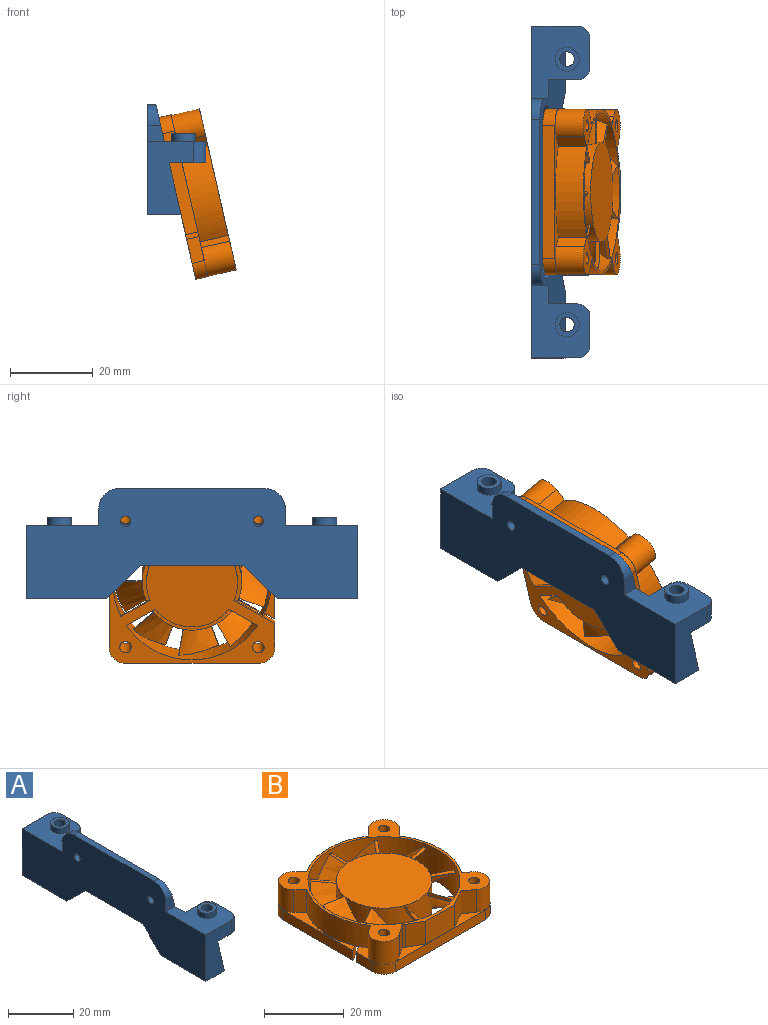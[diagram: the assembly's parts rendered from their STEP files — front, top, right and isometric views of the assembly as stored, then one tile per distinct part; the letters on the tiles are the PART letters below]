
ASSEMBLY  parts=2 mates=1
PART A: 45 faces, bbox 14.7x80.1x28.5 mm
  f0: plane 80.12x26.62mm, normal (-1,0,0), area 1520.2mm2, adj f2,f3,f6,f7,f8,f9,f10,f11
  f1: plane 80x26.5mm, normal (0.97,0,0.22), area 1152.6mm2, adj f2,f3,f6,f10,f11,f12,f13,f14
  f2: plane 17.5x14mm, normal (0,0,1), area 169.7mm2, adj f0,f1,f12,f13,f20,f21,f28,f41
  f3: plane 17.5x14mm, normal (0,0,1), area 169.7mm2, adj f0,f1,f6,f10,f16,f18,f26,f43
  f4: cylinder r=1.75mm len=4.5mm, axis (0,0,1), area 49.5mm2, adj f25,f29
  f5: cylinder r=1.75mm len=4.5mm, axis (0,0,1), area 49.5mm2, adj f22,f27
  f6: plane 17.5x11mm, normal (0,-1,0), area 137.1mm2, adj f0,f1,f3,f15,f17,f43
  f7: plane 8.01x8.01mm, normal (0,0.71,-0.71), area 53.3mm2, adj f0,f8,f15,f37,f38
  f8: plane 25x3.66mm, normal (0,0,-1), area 91.6mm2, adj f0,f7,f9,f37
  f9: plane 8.01x8.01mm, normal (0,-0.71,-0.71), area 53.3mm2, adj f0,f8,f11,f36,f37
  f10: plane 4x4mm, normal (0,-1,0), area 14.2mm2, adj f0,f1,f3,f35
  f11: plane 19.5x8mm, normal (0,0,-1), area 154.2mm2, adj f0,f1,f9,f12,f36
  f12: plane 17.5x11mm, normal (0,1,0), area 137.1mm2, adj f0,f1,f2,f11,f19,f42
  f13: plane 4x4mm, normal (0,1,0), area 14.2mm2, adj f0,f1,f2,f34
  f14: plane 35x1.94mm, normal (0,0,1), area 68mm2, adj f0,f1,f34,f35
  f15: plane 19.5x8mm, normal (0,0,-1), area 154.2mm2, adj f0,f1,f6,f7,f38
  f16: plane 7x5mm, normal (0,1,0), area 32.1mm2, adj f1,f3,f17,f44
  f17: plane 13x8.86mm, normal (0,0,-1), area 78.1mm2, adj f1,f6,f16,f18,f23,f43,f44
  f18: plane 7x5mm, normal (1,0,0), area 35mm2, adj f3,f17,f43,f44
  f19: plane 13x8.86mm, normal (0,0,-1), area 78.1mm2, adj f1,f12,f20,f21,f24,f41,f42
  f20: plane 7x5mm, normal (0,-1,0), area 32.1mm2, adj f1,f2,f19,f41
  f21: plane 7x5mm, normal (1,0,0), area 35mm2, adj f2,f19,f41,f42
  f22: plane 6.5x6.5mm, normal (0,0,-1), area 23.6mm2, adj f5,f23
  f23: cylinder r=3.25mm len=6.5mm, axis (0,0,-1), area 51.1mm2, adj f17,f22
  f24: cylinder r=3.25mm len=6.5mm, axis (0,0,-1), area 51.1mm2, adj f19,f25
  f25: plane 6.5x6.5mm, normal (0,0,-1), area 23.6mm2, adj f4,f24
  f26: cylinder r=2.9mm len=5.8mm, axis (0,0,-1), area 36.4mm2, adj f3,f27
  f27: plane 5.8x5.8mm, normal (0,0,1), area 16.8mm2, adj f5,f26
  f28: cylinder r=2.9mm len=5.8mm, axis (0,0,-1), area 36.4mm2, adj f2,f29
  f29: plane 5.8x5.8mm, normal (0,0,1), area 16.8mm2, adj f4,f28
  f30: cylinder r=5mm len=10.24mm, axis (0.97,0,0.22), area 69.1mm2, adj f1,f31
  f31: plane 10x9.75mm, normal (0.97,0,0.22), area 73.6mm2, adj f30,f40
  f32: cylinder r=5mm len=10.24mm, axis (0.97,0,0.22), area 69.1mm2, adj f1,f33
  f33: plane 10x9.75mm, normal (0.97,0,0.22), area 73.6mm2, adj f32,f39
  f34: cylinder r=5mm len=5mm, axis (-1,0,0), area 18.5mm2, adj f0,f1,f13,f14
  f35: cylinder r=5mm len=5mm, axis (-1,0,0), area 18.5mm2, adj f0,f1,f10,f14
  f36: cylinder r=2mm len=12.31mm, axis (-0.16,-0.7,0.7), area 44.3mm2, adj f1,f9,f11,f37
  f37: cylinder r=2mm len=26.66mm, axis (0,-1,0), area 91.6mm2, adj f1,f7,f8,f9,f36,f38
  f38: cylinder r=2mm len=12.31mm, axis (0.16,-0.7,-0.7), area 44.3mm2, adj f1,f7,f15,f37
  f39: cylinder r=1.25mm len=2.82mm, axis (0.97,0,0.22), area 11.4mm2, adj f0,f33
  f40: cylinder r=1.25mm len=2.82mm, axis (0.97,0,0.22), area 11.4mm2, adj f0,f31
  f41: cylinder r=3mm len=5mm, axis (0,0,-1), area 23.6mm2, adj f2,f19,f20,f21
  f42: cylinder r=3mm len=5mm, axis (0,0,1), area 23.6mm2, adj f2,f12,f19,f21
  f43: cylinder r=3mm len=5mm, axis (0,0,-1), area 23.6mm2, adj f3,f6,f17,f18
  f44: cylinder r=3mm len=5mm, axis (0,0,1), area 23.6mm2, adj f3,f16,f17,f18
PART B: 104 faces, bbox 40x40x10 mm
  f0: plane 4.98x4.18mm, normal (0.64,0.77,0), area 6.5mm2, adj f2,f3,f4,f24
  f1: plane 6.11x2.22mm, normal (-0.94,-0.34,0), area 6.5mm2, adj f2,f3,f4,f5
  f2: bspline ~9x7.84mm, area 9.7mm2, adj f0,f1,f3,f4
  f3: bspline ~10.07x9.67mm, area 73.6mm2, adj f0,f1,f2,f24
  f4: bspline ~10.07x9.67mm, area 73.6mm2, adj f0,f1,f2,f5
  f5: cylinder r=12mm len=13.3mm, axis (0,0,-1), area 69.1mm2, adj f1,f4,f6,f9,f74,f75
  f6: plane 6.4x1.13mm, normal (0.98,0.17,0), area 6.5mm2, adj f5,f8,f9,f10
  f7: plane 6.11x2.22mm, normal (-0.94,0.34,0), area 6.5mm2, adj f8,f9,f10,f11
  f8: bspline ~9.54x9mm, area 9.7mm2, adj f6,f7,f9,f10
  f9: bspline ~9.54x8mm, area 73.6mm2, adj f5,f6,f7,f8
  f10: bspline ~9.54x8mm, area 73.6mm2, adj f6,f7,f8,f11
  f11: cylinder r=12mm len=12.48mm, axis (0,0,-1), area 69.1mm2, adj f7,f10,f12,f15,f74,f75
  f12: plane 5.63x3.25mm, normal (0.87,-0.5,0), area 6.5mm2, adj f11,f14,f15,f16
  f13: plane 5.63x3.25mm, normal (-0.5,0.87,0), area 6.5mm2, adj f14,f15,f16,f17
  f14: bspline ~9x6.77mm, area 9.7mm2, adj f12,f13,f15,f16
  f15: bspline ~10.02x10.02mm, area 73.6mm2, adj f11,f12,f13,f14
  f16: bspline ~10.02x10.02mm, area 73.6mm2, adj f12,f13,f14,f17
  f17: cylinder r=12mm len=12.48mm, axis (0,0,-1), area 69.1mm2, adj f13,f16,f18,f21,f25,f74,f75,f76
  f18: plane 6.11x2.22mm, normal (0.34,-0.94,0), area 6.5mm2, adj f17,f20,f21,f22
  f19: plane 6.4x1.13mm, normal (0.17,0.98,0), area 6.5mm2, adj f20,f21,f22,f24
  f20: bspline ~9.54x9mm, area 9.7mm2, adj f18,f19,f21,f22
  f21: bspline ~9.54x8mm, area 73.6mm2, adj f17,f18,f19,f20
  f22: bspline ~9.54x8mm, area 73.6mm2, adj f18,f19,f20,f24
  f23: plane 5.9x3mm, normal (-1,0,0), area 17.7mm2, adj f39,f40,f52,f72
  f24: cylinder r=12mm len=24mm, axis (0,0,-1), area 416.7mm2, adj f0,f3,f19,f22,f26,f27,f73,f74
  f25: plane 7.42x5.73mm, normal (0,0,1), area 17.8mm2, adj f17,f28,f71,f72
  f26: plane 7.42x5.73mm, normal (0,0,1), area 17.8mm2, adj f24,f28,f69,f70
  f27: plane 7.17x2.5mm, normal (0,0,1), area 17.8mm2, adj f24,f28,f66,f67
  f28: cylinder r=19.1mm len=38.2mm, axis (0,0,1), area 1189.6mm2, adj f25,f26,f27,f33,f40,f66,f67,f69
  f29: cylinder r=11mm len=17.68mm, axis (0,0,-1), area 20.5mm2, adj f40,f70,f71,f74
  f30: cylinder r=11mm len=15.31mm, axis (0,0,-1), area 20.5mm2, adj f40,f67,f69,f73
  f31: plane 32x3mm, normal (0,1,0), area 96mm2, adj f36,f38,f40,f52
  f32: plane 32x3mm, normal (0,-1,0), area 96mm2, adj f35,f39,f40,f52
  f33: plane 39.8x39.8mm, normal (0,0,1), area 255.1mm2, adj f28,f41,f42,f43,f44,f45,f46,f47
  f34: plane 32x3mm, normal (1,0,0), area 96mm2, adj f35,f36,f40,f52
  f35: cylinder r=4mm len=4mm, axis (0,0,-1), area 18.8mm2, adj f32,f34,f40,f52
  f36: cylinder r=4mm len=4mm, axis (0,0,-1), area 18.8mm2, adj f31,f34,f40,f52
  f37: plane 24.95x3mm, normal (-1,0,0), area 74.8mm2, adj f38,f40,f52,f103
  f38: cylinder r=4mm len=4mm, axis (0,0,-1), area 18.8mm2, adj f31,f37,f40,f52
  f39: cylinder r=4mm len=4mm, axis (0,0,-1), area 18.8mm2, adj f23,f32,f40,f52
  f40: plane 40x40mm, normal (0,0,-1), area 853.4mm2, adj f23,f28,f29,f30,f31,f32,f34,f35
  f41: cylinder r=3.9mm len=7.09mm, axis (0,0,1), area 85.8mm2, adj f33,f42,f51,f52
  f42: plane 7x3.35mm, normal (0.57,-0.82,0), area 28.6mm2, adj f33,f41,f43,f52
  f43: cylinder r=19.8mm len=7mm, axis (0,0,1), area 5.8mm2, adj f33,f42,f44,f52
  f44: plane 7x4.69mm, normal (-0.49,-0.87,0), area 37.7mm2, adj f33,f43,f45,f52
  f45: plane 10x7mm, normal (0,-1,0), area 70mm2, adj f33,f44,f52,f59
  f46: cylinder r=19.8mm len=21.94mm, axis (0,0,1), area 162.8mm2, adj f33,f47,f52,f58
  f47: plane 7x2.27mm, normal (0.71,0.71,0), area 22.5mm2, adj f33,f46,f48,f52
  f48: cylinder r=3.9mm len=7mm, axis (0,0,1), area 85.8mm2, adj f33,f47,f49,f52
  f49: plane 7x2.27mm, normal (-0.71,-0.71,0), area 22.5mm2, adj f33,f48,f50,f52
  f50: cylinder r=19.8mm len=22.35mm, axis (0,0,1), area 166.2mm2, adj f33,f49,f51,f52,f102
  f51: plane 7x2.04mm, normal (-0.57,0.82,0), area 17.4mm2, adj f33,f41,f50,f52
  f52: plane 40x40mm, normal (0,0,1), area 158.1mm2, adj f23,f31,f32,f34,f35,f36,f37,f38
  f53: cylinder r=3.9mm len=7.09mm, axis (0,0,1), area 85.8mm2, adj f33,f52,f54,f61
  f54: plane 7x2.04mm, normal (0.57,0.82,0), area 17.4mm2, adj f33,f52,f53,f55
  f55: cylinder r=19.8mm len=22.35mm, axis (0,0,1), area 166.2mm2, adj f33,f52,f54,f56
  f56: plane 7x2.27mm, normal (0.71,-0.71,0), area 22.5mm2, adj f33,f52,f55,f57
  f57: cylinder r=3.9mm len=7mm, axis (0,0,1), area 85.8mm2, adj f33,f52,f56,f58
  f58: plane 7x2.27mm, normal (-0.71,0.71,0), area 22.5mm2, adj f33,f46,f52,f57
  f59: plane 7x4.69mm, normal (0.49,-0.87,0), area 37.7mm2, adj f33,f45,f52,f60
  f60: cylinder r=19.8mm len=7mm, axis (0,0,1), area 5.8mm2, adj f33,f52,f59,f61
  f61: plane 7x3.35mm, normal (-0.57,-0.82,0), area 28.6mm2, adj f33,f52,f53,f60
  f62: cylinder r=1.4mm len=10mm, axis (0,0,1), area 88mm2, adj f33,f40
  f63: cylinder r=1.4mm len=10mm, axis (0,0,1), area 88mm2, adj f33,f40
  f64: cylinder r=1.4mm len=10mm, axis (0,0,1), area 88mm2, adj f33,f40
  f65: cylinder r=1.4mm len=10mm, axis (0,0,1), area 88mm2, adj f33,f40
  f66: plane 8.13x1mm, normal (-1,0,0), area 8.1mm2, adj f27,f28,f40,f68,f76
  f67: plane 8.13x1mm, normal (1,0,0), area 8.1mm2, adj f27,f28,f30,f40,f73
  f68: cylinder r=11mm len=15.31mm, axis (0,0,-1), area 20.5mm2, adj f40,f66,f72,f76
  f69: plane 7.04x4.07mm, normal (0.5,0.87,0), area 8.1mm2, adj f26,f28,f30,f40,f73
  f70: plane 7.04x4.07mm, normal (-0.5,-0.87,0), area 8.1mm2, adj f26,f28,f29,f40,f74
  f71: plane 7.04x4.07mm, normal (0.5,-0.87,0), area 8.1mm2, adj f25,f28,f29,f40,f74
  f72: plane 9.91x5.72mm, normal (-0.5,0.87,0), area 18.1mm2, adj f23,f25,f28,f40,f52,f68,f76,f102
  f73: plane 16.82x10.75mm, normal (0,0,-1), area 21.6mm2, adj f24,f30,f67,f69
  f74: plane 19.42x5.45mm, normal (0,0,-1), area 21.6mm2, adj f5,f11,f17,f24,f29,f70,f71
  f75: plane 24x24mm, normal (0,0,1), area 452.4mm2, adj f5,f11,f17,f24
  f76: plane 16.82x10.75mm, normal (0,0,-1), area 21.6mm2, adj f17,f24,f66,f68,f72
  f77: plane 6.5x1mm, normal (0,1,0), area 6.5mm2, adj f24,f78,f79,f80
  f78: bspline ~9.25x9mm, area 9.3mm2, adj f77,f79,f80,f101
  f79: bspline ~9.25x8.11mm, area 66mm2, adj f24,f77,f78,f101
  f80: bspline ~9.25x8.11mm, area 73.6mm2, adj f24,f77,f78,f101
  f81: plane 4.98x4.18mm, normal (-0.64,0.77,0), area 6.5mm2, adj f24,f82,f83,f84
  f82: bspline ~9x8.68mm, area 9.3mm2, adj f81,f83,f84,f97
  f83: bspline ~9.81x9.03mm, area 66mm2, adj f24,f81,f82,f97
  f84: bspline ~9.81x9.03mm, area 73.6mm2, adj f24,f81,f82,f97
  f85: plane 6.4x1.13mm, normal (-0.98,0.17,0), area 6.5mm2, adj f24,f86,f87,f88
  f86: bspline ~9x8.68mm, area 9.3mm2, adj f85,f87,f88,f98
  f87: bspline ~9.81x9.03mm, area 66mm2, adj f24,f85,f86,f98
  f88: bspline ~9.81x9.03mm, area 73.6mm2, adj f24,f85,f86,f98
  f89: plane 5.63x3.25mm, normal (-0.87,-0.5,0), area 6.5mm2, adj f24,f90,f91,f92
  f90: bspline ~9.25x9mm, area 9.3mm2, adj f89,f91,f92,f99
  f91: bspline ~8.72x8.09mm, area 66mm2, adj f24,f89,f90,f99
  f92: bspline ~9.25x8.11mm, area 73.6mm2, adj f24,f89,f90,f99
  f93: plane 6.11x2.22mm, normal (-0.34,-0.94,0), area 6.5mm2, adj f24,f94,f95,f96
  f94: bspline ~9x7.84mm, area 9.3mm2, adj f93,f95,f96,f100
  f95: bspline ~10.07x9.67mm, area 66mm2, adj f24,f93,f94,f100
  f96: bspline ~10.07x9.67mm, area 73.6mm2, adj f24,f93,f94,f100
  f97: bspline ~8.36x2.24mm, area 6.5mm2, adj f24,f82,f83,f84
  f98: bspline ~6.89x5.95mm, area 6.5mm2, adj f24,f86,f87,f88
  f99: bspline ~8.36x1.01mm, area 6.5mm2, adj f24,f90,f91,f92
  f100: bspline ~6.89x5.96mm, area 6.5mm2, adj f24,f94,f95,f96
  f101: bspline ~7.6x4.83mm, area 6.5mm2, adj f24,f78,f79,f80
  f102: plane 1.26x1.03mm, normal (0,0,-1), area 0.7mm2, adj f28,f50,f72,f103
  f103: plane 3x2.45mm, normal (0.5,-0.87,0), area 8.5mm2, adj f28,f37,f40,f52,f102
PLACE A t=(0,0,-12.98)mm
PLACE B rot(axis=(0.53,0.53,0.66),112.9deg) t=(7.12,0,-9.13)mm
MATE slider A.f39 <-> B.f38  axis (0.97,0,0.22) through (3.55,-16,6.47)mm
